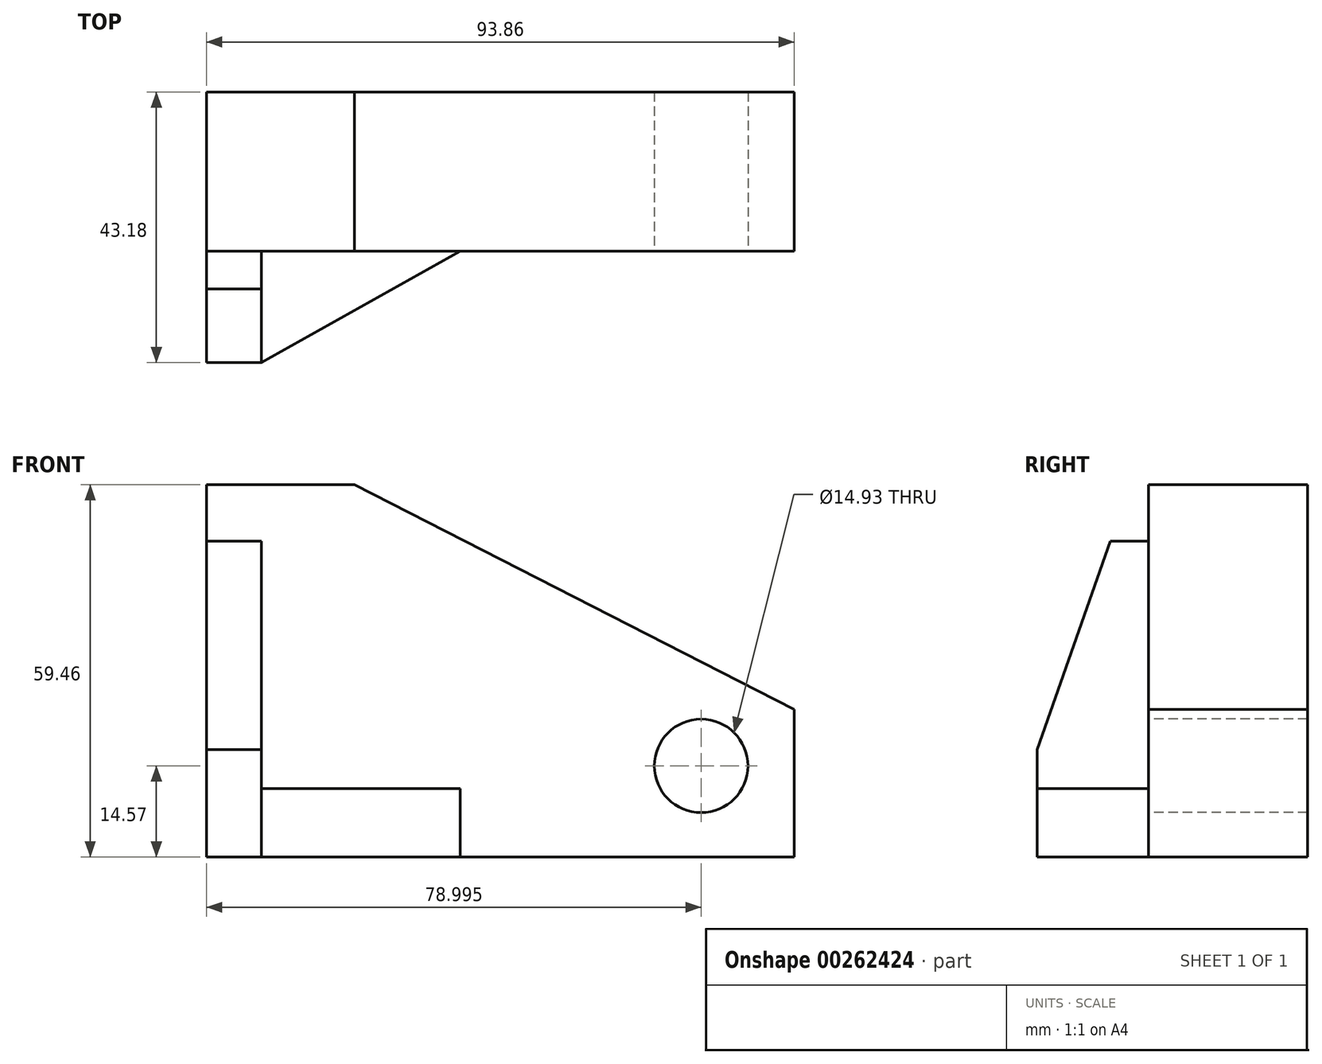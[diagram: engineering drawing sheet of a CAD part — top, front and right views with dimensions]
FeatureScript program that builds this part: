
annotation { "Feature Type Name" : "Feature", "Feature Type Description" : "" }
export const myFeature = defineFeature(function(context is Context, id is Id, definition is map)
    precondition{}
    {
        {
            var Q0;
            Q0=qCreatedBy(makeId("Front.planeOp"),FACE);
            var sketch = newSketch(context, id + "F0", { "sketchPlane" : qUnion([Q0])});
            skLineSegment(sketch, "E0.bottom", {"start": v(-40.52, 30.17) * mm, "end": v(53.34, 30.17) * mm});
            skLineSegment(sketch, "E0.top", {"start": v(-40.52, -29.3) * mm, "end": v(53.34, -29.3) * mm});
            skLineSegment(sketch, "E0.left", {"start": v(-40.52, 30.17) * mm, "end": v(-40.52, -29.3) * mm});
            skLineSegment(sketch, "E0.right", {"start": v(53.34, 30.17) * mm, "end": v(53.34, -29.3) * mm});
            skSolve(sketch);
        }
        {
            var Q0;
            Q0 = qSketchRegion(id + "F0", true);
            extrude(context, id + "F1", {"entities" : qUnion([Q0]), "depth" : 25.4 * mm});
        }
        {
            var Q0;
            Q0=makeQuery(id+"F1.opExtrude","CAP_FACE",FACE,{"disambiguationData":[OSD([sQuery(id+"F0.wireOp",EDGE,"E0.bottom"),sQuery(id+"F0.wireOp",EDGE,"E0.top"),sQuery(id+"F0.wireOp",EDGE,"E0.left"),sQuery(id+"F0.wireOp",EDGE,"E0.right")])],"isStart":false});
            var sketch = newSketch(context, id + "F2", { "sketchPlane" : qUnion([Q0])});
            skLineSegment(sketch, "E1", {"start": v(-16.9, 30.17) * mm, "end": v(53.34, -5.68) * mm});
            skLineSegment(sketch, "E2", {"start": v(53.34, -5.68) * mm, "end": v(53.34, 30.17) * mm});
            skLineSegment(sketch, "E3", {"start": v(53.34, 30.17) * mm, "end": v(-16.9, 30.17) * mm});
            skSolve(sketch);
        }
        {
            var Q0;
            Q0 = qSketchRegion(id + "F2", true);
            extrude(context, id + "F3", {"entities" : qUnion([Q0]), "operationType" : NewBodyOperationType.REMOVE, "oppositeDirection" : true, "depth" : 25.4 * mm});
        }
        {
            var Q0;
            Q0=makeQuery(id+"F1.opExtrude","CAP_FACE",FACE,{"disambiguationData":[OSD([sQuery(id+"F0.wireOp",EDGE,"E0.bottom"),sQuery(id+"F0.wireOp",EDGE,"E0.top"),sQuery(id+"F0.wireOp",EDGE,"E0.left"),sQuery(id+"F0.wireOp",EDGE,"E0.right")])],"isStart":false});
            var sketch = newSketch(context, id + "F4", { "sketchPlane" : qUnion([Q0])});
            skLineSegment(sketch, "E4", {"start": v(-40.52, 21.13) * mm, "end": v(-31.77, 21.13) * mm});
            skLineSegment(sketch, "E5", {"start": v(-31.77, 21.13) * mm, "end": v(-31.77, -29.3) * mm});
            skLineSegment(sketch, "E6", {"start": v(-31.77, -29.3) * mm, "end": v(-40.52, -29.3) * mm});
            skLineSegment(sketch, "E7", {"start": v(-40.52, -29.3) * mm, "end": v(-40.52, 21.13) * mm});
            skSolve(sketch);
        }
        {
            var Q0;
            Q0 = qSketchRegion(id + "F4", true);
            extrude(context, id + "F5", {"entities" : qUnion([Q0]), "operationType" : NewBodyOperationType.ADD, "depth" : 17.78 * mm});
        }
        {
            var Q0;
            Q0=makeQuery(id+"F5.opExtrude","SWEPT_FACE",FACE,{"disambiguationData":[OSD([sQuery(id+"F4.wireOp",EDGE,"E5")])]});
            var sketch = newSketch(context, id + "F6", { "sketchPlane" : qUnion([Q0])});
            skLineSegment(sketch, "E8", {"start": v(-31.46, 21.13) * mm, "end": v(-43.18, -12.12) * mm});
            skLineSegment(sketch, "E9", {"start": v(-43.18, -12.12) * mm, "end": v(-43.18, 21.13) * mm});
            skLineSegment(sketch, "E10", {"start": v(-43.18, 21.13) * mm, "end": v(-31.46, 21.13) * mm});
            skSolve(sketch);
        }
        {
            var Q0;
            Q0 = qSketchRegion(id + "F6", true);
            extrude(context, id + "F7", {"entities" : qUnion([Q0]), "operationType" : NewBodyOperationType.REMOVE, "oppositeDirection" : true, "depth" : 25.4 * mm});
        }
        {
            var Q0;
            Q0=makeQuery(id+"F5.boolean.opBoolean","MERGE",FACE,{"derivedFrom":[makeQuery(id+"F1.opExtrude","SWEPT_FACE",FACE,{"disambiguationData":[OSD([sQuery(id+"F0.wireOp",EDGE,"E0.top")])]}),makeQuery(id+"F5.opExtrude","SWEPT_FACE",FACE,{"disambiguationData":[OSD([sQuery(id+"F4.wireOp",EDGE,"E6")])]})]});
            var sketch = newSketch(context, id + "F8", { "sketchPlane" : qUnion([Q0])});
            skLineSegment(sketch, "E11", {"start": v(-31.77, 43.18) * mm, "end": v(0, 25.4) * mm});
            skLineSegment(sketch, "E12", {"start": v(0, 25.4) * mm, "end": v(-31.77, 25.4) * mm});
            skLineSegment(sketch, "E13", {"start": v(-31.77, 25.4) * mm, "end": v(-31.77, 43.18) * mm});
            skSolve(sketch);
        }
        {
            var Q0;
            Q0 = qSketchRegion(id + "F8", true);
            extrude(context, id + "F9", {"entities" : qUnion([Q0]), "operationType" : NewBodyOperationType.ADD, "oppositeDirection" : true, "depth" : 10.92 * mm});
        }
        {
            var Q0;
            Q0=makeQuery(id+"F1.opExtrude","CAP_FACE",FACE,{"disambiguationData":[OSD([sQuery(id+"F0.wireOp",EDGE,"E0.bottom"),sQuery(id+"F0.wireOp",EDGE,"E0.top"),sQuery(id+"F0.wireOp",EDGE,"E0.left"),sQuery(id+"F0.wireOp",EDGE,"E0.right")])],"isStart":false});
            var sketch = newSketch(context, id + "F10", { "sketchPlane" : qUnion([Q0])});
            skCircle(sketch, "E14", {"center": v(38.47, -14.72) * mm, "radius": 7.47 * mm});
            skSolve(sketch);
        }
        {
            var Q0;
            Q0 = qSketchRegion(id + "F10", true);
            extrude(context, id + "F11", {"entities" : qUnion([Q0]), "operationType" : NewBodyOperationType.REMOVE, "oppositeDirection" : true, "depth" : 25.4 * mm});
        }
    });
